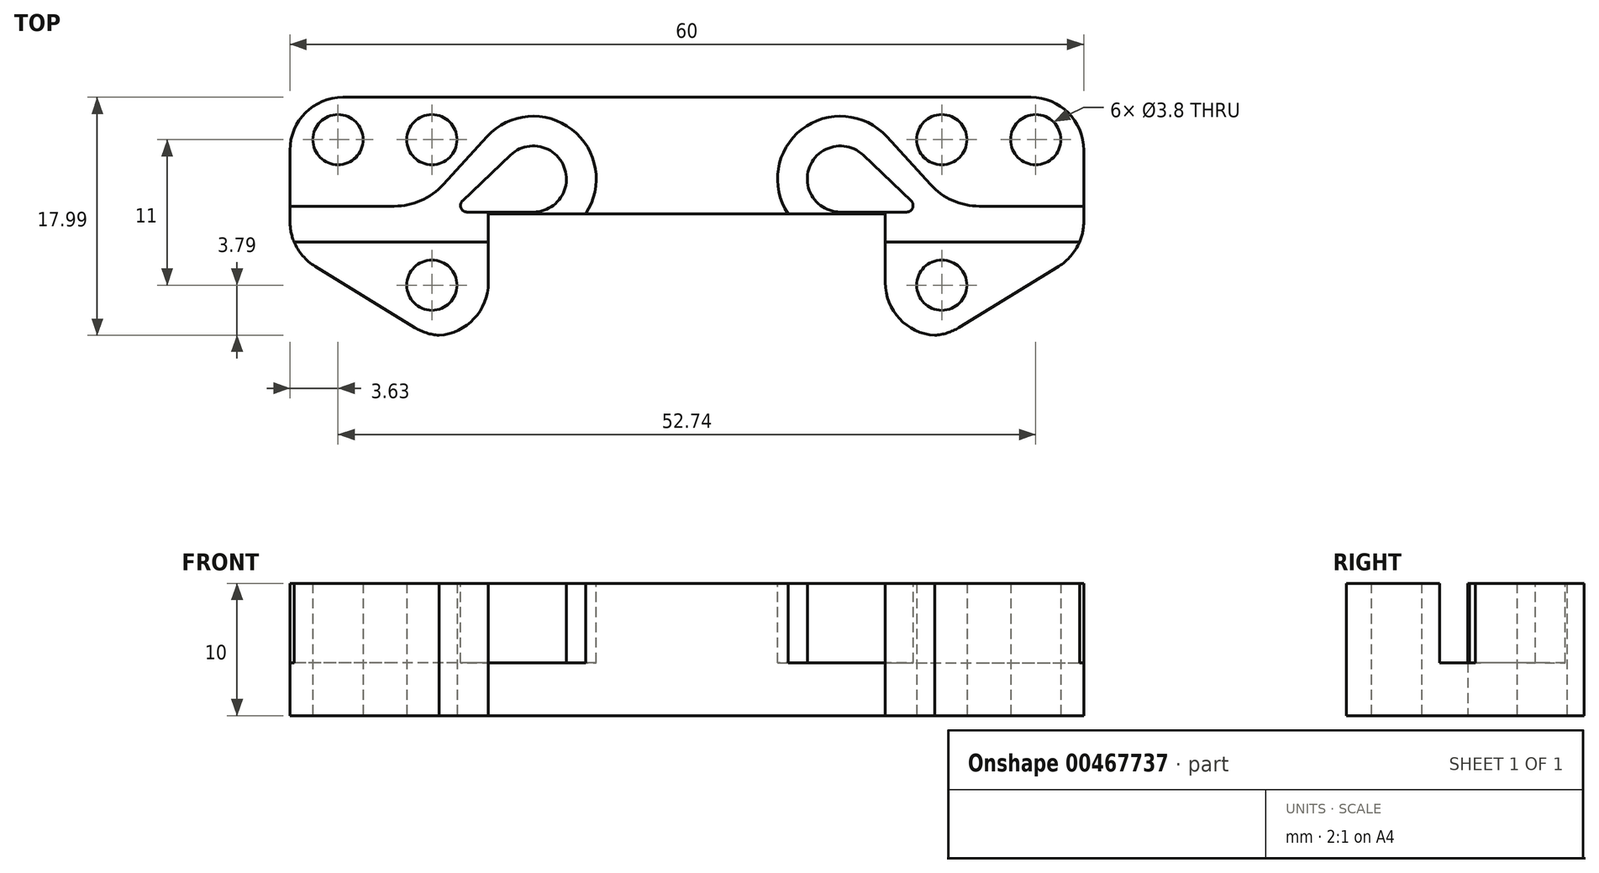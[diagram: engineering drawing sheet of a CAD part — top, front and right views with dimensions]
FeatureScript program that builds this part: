
annotation { "Feature Type Name" : "Feature", "Feature Type Description" : "" }
export const myFeature = defineFeature(function(context is Context, id is Id, definition is map)
    precondition{}
    {
        {
            var Q0;
            Q0=qCreatedBy(makeId("Top.planeOp"),FACE);
            var sketch = newSketch(context, id + "F0", { "sketchPlane" : qUnion([Q0])});
            skLineSegment(sketch, "E0.bottom", {"start": v(0, 9) * mm, "end": v(30, 9) * mm});
            skLineSegment(sketch, "E0.top", {"start": v(0, -9) * mm, "end": v(19.6, -9) * mm});
            skLineSegment(sketch, "E0.left", {"start": v(0, 9) * mm, "end": v(0, -9) * mm});
            skLineSegment(sketch, "E0.right", {"start": v(30, 9) * mm, "end": v(30, -2.62) * mm});
            skLineSegment(sketch, "E1.bottom", {"start": v(0, -1.8) * mm, "end": v(15, -1.8) * mm});
            skLineSegment(sketch, "E1.top", {"start": v(0, -9) * mm, "end": v(15, -9) * mm});
            skLineSegment(sketch, "E1.left", {"start": v(0, -1.8) * mm, "end": v(0, -9) * mm});
            skLineSegment(sketch, "E1.right", {"start": v(15, -1.8) * mm, "end": v(15, -9) * mm});
            skCircle(sketch, "E2", {"center": v(26.37, 5.8) * mm, "radius": 1.9 * mm});
            skCircle(sketch, "E3", {"center": v(19.27, 5.8) * mm, "radius": 1.9 * mm});
            skLineSegment(sketch, "E4", {"start": v(19.27, 5.8) * mm, "end": v(26.37, 5.8) * mm});
            skCircle(sketch, "E5", {"center": v(19.27, -5.2) * mm, "radius": 1.9 * mm});
            skLineSegment(sketch, "E6", {"start": v(19.27, 5.8) * mm, "end": v(19.27, -5.2) * mm});
            skLineSegment(sketch, "E7", {"start": v(19.6, -9) * mm, "end": v(30, -2.62) * mm});
            skSolve(sketch);
        }
        {
            var Q0;
            Q0=makeQuery(id+"F0.imprint","IMPRINT",FACE,{"disambiguationData":[TD([[makeQuery(id+"F0.imprint","IMPRINT",EDGE,{"derivedFrom":sQuery(id+"F0.wireOp",EDGE,"E0.bottom")}),-1.0]])]});
            extrude(context, id + "F1", {"entities" : qUnion([Q0]), "depth" : 10 * mm});
        }
        {
            var Q0;
            Q0=makeQuery(id+"F1.opExtrude","CAP_FACE",FACE,{"disambiguationData":[OSD([sQuery(id+"F0.wireOp",EDGE,"E0.bottom"),sQuery(id+"F0.wireOp",EDGE,"E0.top"),sQuery(id+"F0.wireOp",EDGE,"E0.left"),sQuery(id+"F0.wireOp",EDGE,"E0.right")])],"isStart":false});
            var sketch = newSketch(context, id + "F2", { "sketchPlane" : qUnion([Q0])});
            skCircle(sketch, "E8", {"center": v(11.6, 2.83) * mm, "radius": 2.5 * mm});
            skCircle(sketch, "E9", {"center": v(16.6, 0.83) * mm, "radius": 0.5 * mm});
            skLineSegment(sketch, "E10", {"start": v(13.33, 4.64) * mm, "end": v(16.95, 1.19) * mm});
            skLineSegment(sketch, "E11", {"start": v(16.6, 0.33) * mm, "end": v(11.6, 0.33) * mm});
            skCircle(sketch, "E12", {"center": v(11.6, 2.83) * mm, "radius": 4.75 * mm});
            skLineSegment(sketch, "E13.bottom", {"start": v(19.9, 0.78) * mm, "end": v(31.09, 0.78) * mm});
            skLineSegment(sketch, "E13.top", {"start": v(19.9, -1.92) * mm, "end": v(31.09, -1.92) * mm});
            skLineSegment(sketch, "E13.left", {"start": v(19.9, 0.78) * mm, "end": v(19.9, -1.92) * mm});
            skLineSegment(sketch, "E13.right", {"start": v(31.09, 0.78) * mm, "end": v(31.09, -1.92) * mm});
            skLineSegment(sketch, "E14", {"start": v(15.11, 6.03) * mm, "end": v(19.9, 0.78) * mm});
            skLineSegment(sketch, "E15", {"start": v(11.6, -1.92) * mm, "end": v(19.9, -1.92) * mm});
            skSolve(sketch);
        }
        {
            var Q0;
            {var subQ0=sQuery(id+"F2.wireOp",EDGE,"E10");var subQ1=sQuery(id+"F2.wireOp",EDGE,"E8");var subQ2=makeQuery(id+"F2.imprint","INTERSECT",VERTEX,{"derivedFrom":[subQ1,subQ0]});Q0=makeQuery(id+"F2.imprint","IMPRINT",FACE,{"disambiguationData":[TD([[makeQuery(id+"F2.imprint","IMPRINT",EDGE,{"disambiguationData":[TD([[subQ2,-1.0]])],"derivedFrom":subQ1}),-1.0]])]});}
            var Q1;
            {var subQ0=sQuery(id+"F2.wireOp",EDGE,"E12");var subQ1=sQuery(id+"F2.wireOp",EDGE,"E11");var subQ2=makeQuery(id+"F2.imprint","INTERSECT",VERTEX,{"derivedFrom":[subQ1,subQ0]});Q1=makeQuery(id+"F2.imprint","IMPRINT",FACE,{"disambiguationData":[TD([[makeQuery(id+"F2.imprint","IMPRINT",EDGE,{"disambiguationData":[TD([[subQ2,-1.0]])],"derivedFrom":subQ1}),1.0]])]});}
            var Q2;
            {var subQ5=sQuery(id+"F2.wireOp",EDGE,"E13.left");Q2=makeQuery(id+"F2.imprint","IMPRINT",FACE,{"disambiguationData":[TD([[makeQuery(id+"F2.imprint","IMPRINT",EDGE,{"derivedFrom":subQ5}),-1.0]])]});}
            var Q3;
            {var subQ0=sQuery(id+"F2.wireOp",EDGE,"E13.left");Q3=makeQuery(id+"F2.imprint","IMPRINT",FACE,{"disambiguationData":[TD([[makeQuery(id+"F2.imprint","IMPRINT",EDGE,{"derivedFrom":subQ0}),1.0]])]});}
            extrude(context, id + "F3", {"entities" : qUnion([Q0, Q1, Q2, Q3]), "operationType" : NewBodyOperationType.REMOVE, "oppositeDirection" : true, "depth" : 6 * mm});
        }
        {
            var Q0;
            Q0=makeQuery(id+"F3.boolean.opBoolean","COPY",EDGE,{"derivedFrom":makeQuery(id+"F3.opExtrude","SWEPT_EDGE",EDGE,{"disambiguationData":[OSD([sQuery(id+"F2.wireOp",EDGE,"E13.bottom"),sQuery(id+"F2.wireOp",EDGE,"E13.left"),sQuery(id+"F2.wireOp",EDGE,"E14")])]})});
            fillet(context, id + "F4", {"entities" : qUnion([Q0]), "radius" : 5 * mm, "tangentPropagation" : true, "allowEdgeOverflow" : false});
        }
        {
            var Q0;
            Q0=makeQuery(id+"F1.opExtrude","SWEPT_EDGE",EDGE,{"disambiguationData":[OSD([sQuery(id+"F0.wireOp",EDGE,"E0.right"),sQuery(id+"F0.wireOp",EDGE,"E7")])]});
            var Q1;
            Q1=makeQuery(id+"F1.opExtrude","SWEPT_EDGE",EDGE,{"disambiguationData":[OSD([sQuery(id+"F0.wireOp",EDGE,"E0.top"),sQuery(id+"F0.wireOp",EDGE,"E7")])]});
            var Q2;
            Q2=makeQuery(id+"F1.opExtrude","SWEPT_EDGE",EDGE,{"disambiguationData":[OSD([sQuery(id+"F0.wireOp",EDGE,"E0.top"),sQuery(id+"F0.wireOp",EDGE,"E1.top"),sQuery(id+"F0.wireOp",EDGE,"E1.right")])]});
            var Q3;
            Q3=makeQuery(id+"F1.opExtrude","SWEPT_EDGE",EDGE,{"disambiguationData":[OSD([sQuery(id+"F0.wireOp",EDGE,"E0.bottom"),sQuery(id+"F0.wireOp",EDGE,"E0.right")])]});
            fillet(context, id + "F5", {"entities" : qUnion([Q0, Q1, Q2, Q3]), "radius" : 4 * mm, "tangentPropagation" : true, "allowEdgeOverflow" : false});
        }
        {
            var Q0;
            Q0=makeQuery(id+"F1.opExtrude","SWEPT_FACE",FACE,{"disambiguationData":[OSD([sQuery(id+"F0.wireOp",EDGE,"E1.bottom")])]});
            var sketch = newSketch(context, id + "F6", { "sketchPlane" : qUnion([Q0])});
            skLineSegment(sketch, "E16.bottom", {"start": v(0, 0) * mm, "end": v(15, 0) * mm});
            skLineSegment(sketch, "E16.top", {"start": v(0, 10) * mm, "end": v(15, 10) * mm});
            skLineSegment(sketch, "E16.left", {"start": v(0, 0) * mm, "end": v(0, 10) * mm});
            skLineSegment(sketch, "E16.right", {"start": v(15, 0) * mm, "end": v(15, 10) * mm});
            skSolve(sketch);
        }
        {
            var Q0;
            Q0=makeQuery(id+"F6.imprint","IMPRINT",FACE,{"disambiguationData":[TD([[makeQuery(id+"F6.imprint","IMPRINT",EDGE,{"derivedFrom":sQuery(id+"F6.wireOp",EDGE,"E16.bottom")}),1.0]])]});
            extrude(context, id + "F7", {"entities" : qUnion([Q0]), "operationType" : NewBodyOperationType.REMOVE, "oppositeDirection" : true, "depth" : 2 * mm});
        }
        {
            var Q0;
            Q0=makeQuery(id+"F1.opExtrude","SWEPT_BODY",BODY,{"disambiguationData":[OSD([sQuery(id+"F0.wireOp",EDGE,"E0.bottom"),sQuery(id+"F0.wireOp",EDGE,"E0.top"),sQuery(id+"F0.wireOp",EDGE,"E0.left"),sQuery(id+"F0.wireOp",EDGE,"E0.right"),sQuery(id+"F0.wireOp",EDGE,"E1.bottom"),sQuery(id+"F0.wireOp",EDGE,"E1.right"),sQuery(id+"F0.wireOp",EDGE,"E2"),sQuery(id+"F0.wireOp",EDGE,"E3"),sQuery(id+"F0.wireOp",EDGE,"E5"),sQuery(id+"F0.wireOp",EDGE,"E7")])]});
            var Q1;
            Q1=qCreatedBy(makeId("Right.planeOp"),FACE);
            mirror(context, id + "F8", {"operationType" : NewBodyOperationType.ADD, "entities" : qUnion([Q0]), "mirrorPlane" : qUnion([Q1])});
        }
    });
